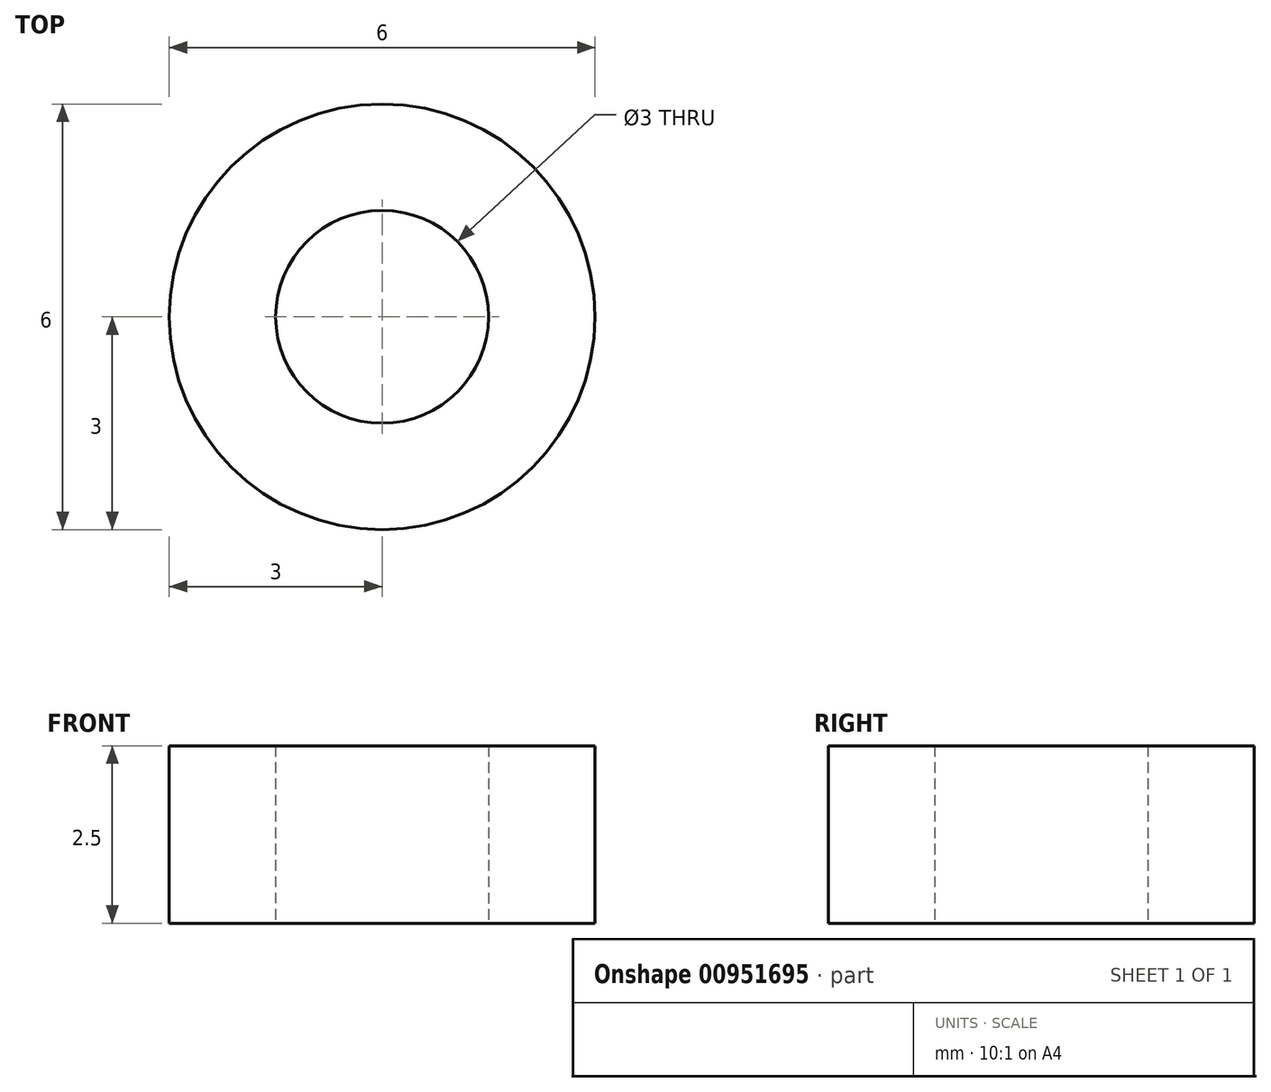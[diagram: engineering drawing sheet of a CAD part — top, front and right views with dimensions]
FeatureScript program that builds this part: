
annotation { "Feature Type Name" : "Feature", "Feature Type Description" : "" }
export const myFeature = defineFeature(function(context is Context, id is Id, definition is map)
    precondition{}
    {
        {
            var Q0;
            Q0=qCreatedBy(makeId("Top.planeOp"), FACE);
            var sketch = newSketch(context, id + "F0", { "sketchPlane" : qUnion([Q0])});
            skCircle(sketch, "E0", {"center": v(0, 0) * mm, "radius": 1.5 * mm});
            skCircle(sketch, "E1", {"center": v(0, 0) * mm, "radius": 3 * mm});
            skSolve(sketch);
        }
        {
            var Q0;
            Q0 = qSketchRegion(id + "F0", true);
            extrude(context, id + "F1", {"entities" : qUnion([Q0]), "domain" : OperationDomain.MODEL, "flatOperationType" : FlatOperationType.REMOVE, "depth" : 2.5 * mm, "offsetDistance" : 25 * mm});
        }
    });
